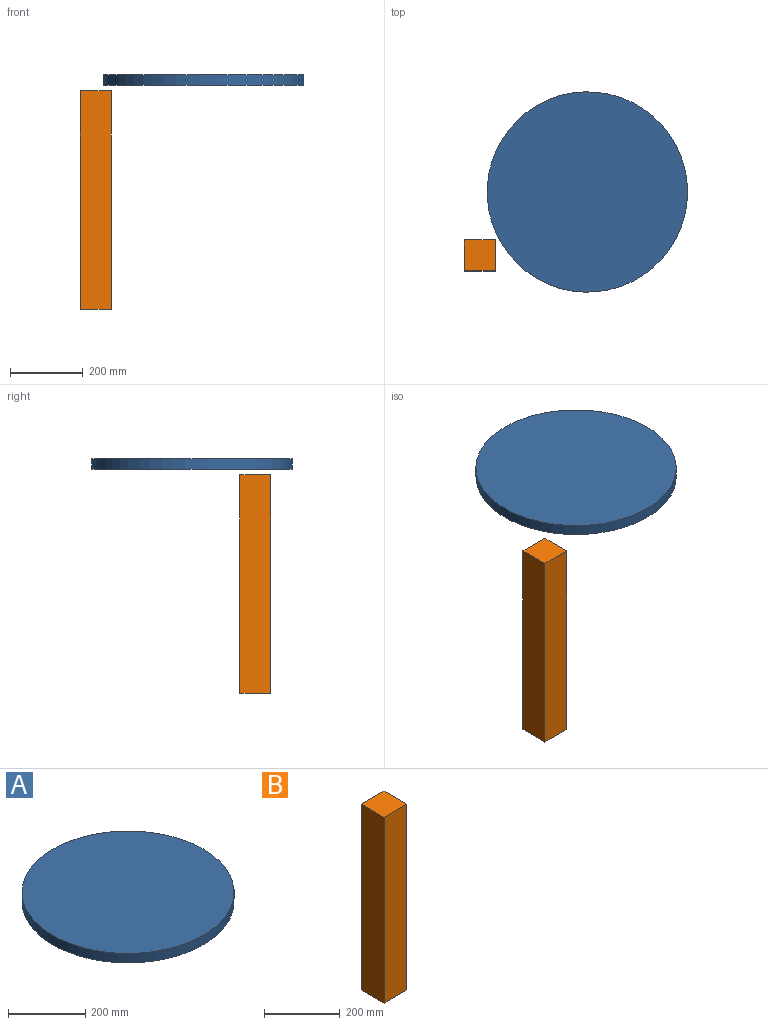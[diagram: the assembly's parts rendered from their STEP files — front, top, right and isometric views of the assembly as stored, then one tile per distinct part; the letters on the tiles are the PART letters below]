
ASSEMBLY  parts=2 mates=1
PART A: 3 faces, bbox 550x550x30 mm
  f0: cylinder r=275mm len=550mm, axis (0,0,-1), area 51836.3mm2, adj f1,f2
  f1: plane 550x550mm, normal (0,0,1), area 237582.9mm2, adj f0
  f2: plane 550x550mm, normal (0,0,-1), area 237582.9mm2, adj f0
PART B: 6 faces, bbox 85x85x600 mm
  f0: plane 600x85mm, normal (-1,0,0), area 51000mm2, adj f1,f3,f4,f5
  f1: plane 600x85mm, normal (0,-1,0), area 51000mm2, adj f0,f2,f4,f5
  f2: plane 600x85mm, normal (1,0,0), area 51000mm2, adj f1,f3,f4,f5
  f3: plane 600x85mm, normal (0,1,0), area 51000mm2, adj f0,f2,f4,f5
  f4: plane 85x85mm, normal (0,0,-1), area 7225mm2, adj f0,f1,f2,f3
  f5: plane 85x85mm, normal (0,0,1), area 7225mm2, adj f0,f1,f2,f3
PLACE A t=(361.42,-62.51,94.57)mm fixed
PLACE B rot(axis=(0,0,-1),0deg) t=(74.24,-242.76,79.67)mm
MATE parallel B.f5 <-> A.f0  axis (0,0,1) through (66.48,-236.34,79.67)mm
